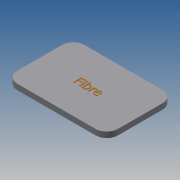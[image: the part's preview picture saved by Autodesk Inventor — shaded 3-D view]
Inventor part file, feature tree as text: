
AUTODESK INVENTOR PART (.ipt)
format: ipt  version: 2016 (Build 200138000, 138)  size: 208,896 bytes
history: native  units: in
note: dims shown in document units (in); Inventor stores cm internally (conversion verified against a paired STEP export)
features: sketch x2, extrude x1, emboss x1
ambient origin geometry x8: Origin, YZ Plane, XZ Plane, XY Plane, X Axis, Y Axis, Z Axis, Center Point
bodies: Solid1 (feature_tree)
feature tree (4):
  extrude  "Extrusion1"  Depth=24.0in
  emboss  "Emboss1"
  sketch  "Sketch1"  dims[d0=36.0in d1=24.0in]
  sketch  "Sketch8"  dims[d2=2.0in d3=0.0in d9=4.0in d53=0.1in d54=0.0in]
